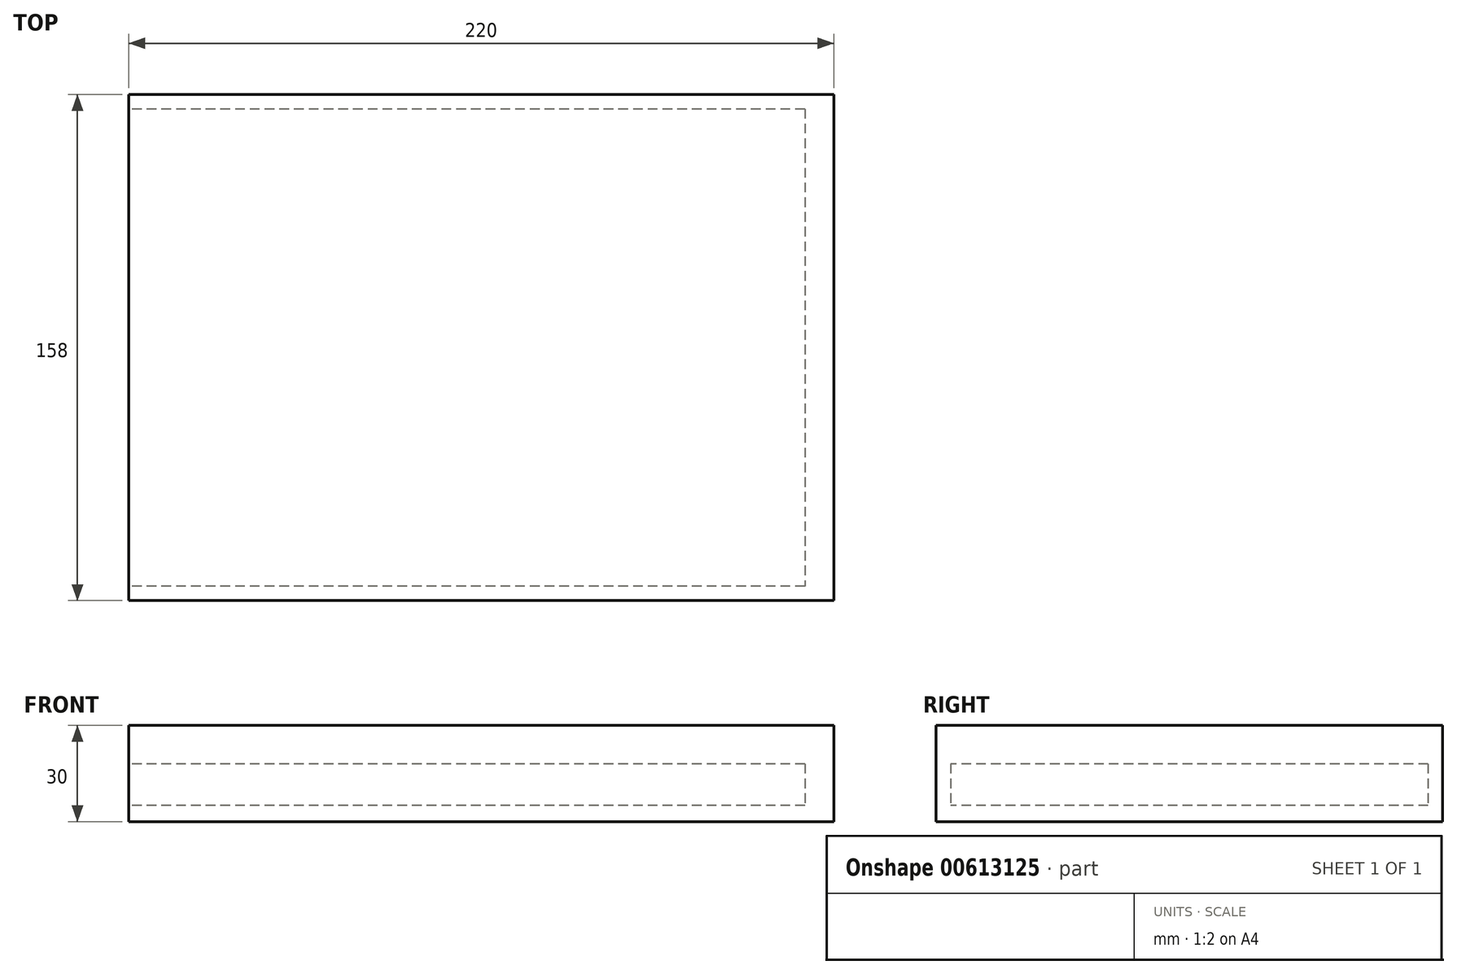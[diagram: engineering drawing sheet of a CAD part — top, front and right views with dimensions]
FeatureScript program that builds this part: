
annotation { "Feature Type Name" : "Feature", "Feature Type Description" : "" }
export const myFeature = defineFeature(function(context is Context, id is Id, definition is map)
    precondition{}
    {
        {
            var Q0;
            Q0=qCreatedBy(makeId("Top.planeOp"),FACE);
            var sketch = newSketch(context, id + "F0", { "sketchPlane" : qUnion([Q0])});
            skLineSegment(sketch, "E0.bottom", {"start": v(-110.57, 85.7) * mm, "end": v(109.43, 85.7) * mm});
            skLineSegment(sketch, "E0.top", {"start": v(-110.57, -72.3) * mm, "end": v(109.43, -72.3) * mm});
            skLineSegment(sketch, "E0.left", {"start": v(-110.57, 85.7) * mm, "end": v(-110.57, -72.3) * mm});
            skLineSegment(sketch, "E0.right", {"start": v(109.43, 85.7) * mm, "end": v(109.43, -72.3) * mm});
            skSolve(sketch);
        }
        {
            var Q0;
            Q0=makeQuery(id+"F0.imprint","IMPRINT",FACE,{"disambiguationData":[TD([[makeQuery(id+"F0.imprint","IMPRINT",EDGE,{"derivedFrom":sQuery(id+"F0.wireOp",EDGE,"E0.bottom")}),-1.0]])]});
            extrude(context, id + "F1", {"entities" : qUnion([Q0]), "depth" : 30 * mm, "offsetDistance" : 25 * mm});
        }
        {
            var Q0;
            Q0=makeQuery(id+"F1.opExtrude","SWEPT_FACE",FACE,{"disambiguationData":[OSD([sQuery(id+"F0.wireOp",EDGE,"E0.left")])]});
            var sketch = newSketch(context, id + "F2", { "sketchPlane" : qUnion([Q0])});
            skLineSegment(sketch, "E1.bottom", {"start": v(-81.2, 18) * mm, "end": v(67.8, 18) * mm});
            skLineSegment(sketch, "E1.top", {"start": v(-81.2, 5) * mm, "end": v(67.8, 5) * mm});
            skLineSegment(sketch, "E1.left", {"start": v(-81.2, 18) * mm, "end": v(-81.2, 5) * mm});
            skLineSegment(sketch, "E1.right", {"start": v(67.8, 18) * mm, "end": v(67.8, 5) * mm});
            skSolve(sketch);
        }
        {
            var Q0;
            Q0 = qSketchRegion(id + "F2", true);
            extrude(context, id + "F3", {"entities" : qUnion([Q0]), "operationType" : NewBodyOperationType.REMOVE, "oppositeDirection" : true, "depth" : 211 * mm, "offsetDistance" : 25 * mm});
        }
    });
